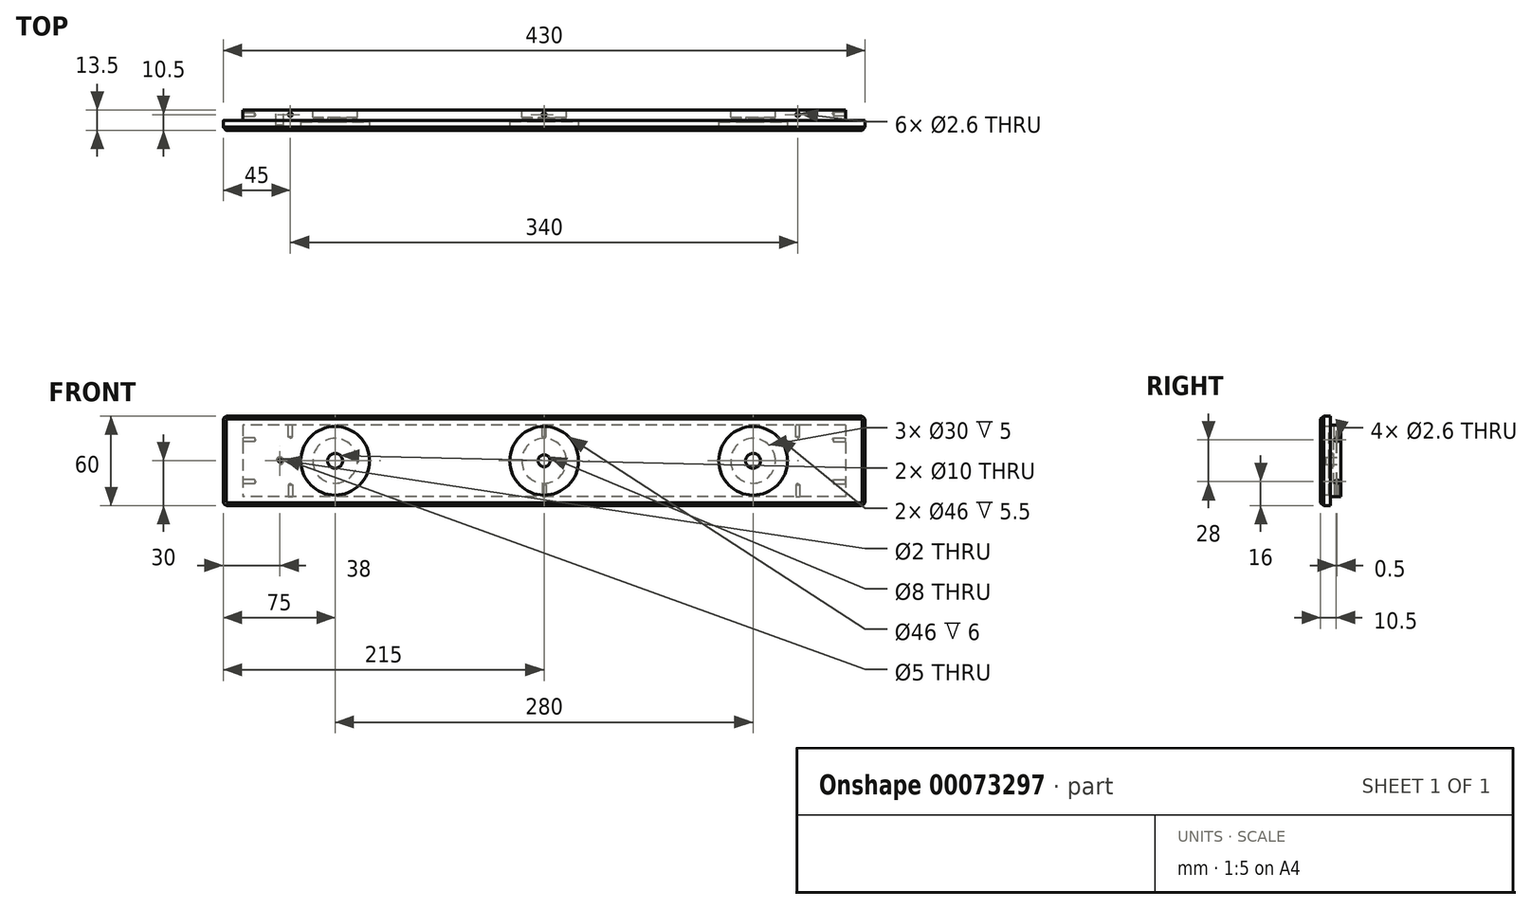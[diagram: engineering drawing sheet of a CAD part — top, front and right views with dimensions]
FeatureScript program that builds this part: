
annotation { "Feature Type Name" : "Feature", "Feature Type Description" : "" }
export const myFeature = defineFeature(function(context is Context, id is Id, definition is map)
    precondition{}
    {
        {
            var Q0;
            Q0=qCreatedBy(makeId("Right.planeOp"),FACE);
            var sketch = newSketch(context, id + "F0", { "sketchPlane" : qUnion([Q0])});
            skPoint(sketch, "E0.rect.middle", {"position": v(0, 0) * mm});
            skLineSegment(sketch, "E1.right", {"start": v(0, 30) * mm, "end": v(0, -30) * mm});
            skLineSegment(sketch, "E2", {"start": v(-6.5, 17.62) * mm, "end": v(-6.5, -17.62) * mm});
            skLineSegment(sketch, "E3", {"start": v(0, 30) * mm, "end": v(0, 24) * mm});
            skLineSegment(sketch, "E4", {"start": v(0, 24) * mm, "end": v(7, 24) * mm});
            skLineSegment(sketch, "E5.MirrorCS", {"start": v(0, -24) * mm, "end": v(7, -24) * mm});
            skLineSegment(sketch, "E6", {"start": v(7, -24) * mm, "end": v(7, 24) * mm});
            skLineSegment(sketch, "E7", {"start": v(0, -30) * mm, "end": v(-6.5, -30) * mm});
            skLineSegment(sketch, "E8", {"start": v(-6.5, -30) * mm, "end": v(-6.5, -16.02) * mm});
            skLineSegment(sketch, "E9", {"start": v(-6.5, 17.62) * mm, "end": v(-6.5, 30) * mm});
            skLineSegment(sketch, "E10", {"start": v(-6.5, 30) * mm, "end": v(0, 30) * mm});
            skSolve(sketch);
        }
        {
            var Q0;
            {var subQ2=sQuery(id+"F0.wireOp",EDGE,"E2");Q0=makeQuery(id+"F0.imprint","IMPRINT",FACE,{"disambiguationData":[TD([[makeQuery(id+"F0.imprint","IMPRINT",EDGE,{"derivedFrom":subQ2}),1.0]])]});}
            extrude(context, id + "F1", {"entities" : qUnion([Q0]), "endBound" : BoundingType.SYMMETRIC, "depth" : 430 * mm});
        }
        {
            var Q0;
            {var subQ2=sQuery(id+"F0.wireOp",EDGE,"E2");Q0=makeQuery(id+"F0.imprint","IMPRINT",FACE,{"disambiguationData":[TD([[makeQuery(id+"F0.imprint","IMPRINT",EDGE,{"derivedFrom":subQ2}),1.0]])]});}
            var Q1;
            {var subQ0=sQuery(id+"F0.wireOp",EDGE,"E4");Q1=makeQuery(id+"F0.imprint","IMPRINT",FACE,{"disambiguationData":[TD([[makeQuery(id+"F0.imprint","IMPRINT",EDGE,{"derivedFrom":subQ0}),-1.0]])]});}
            extrude(context, id + "F2", {"entities" : qUnion([Q0, Q1]), "operationType" : NewBodyOperationType.ADD, "endBound" : BoundingType.SYMMETRIC, "depth" : 404 * mm});
        }
        {
            var Q0;
            Q0=makeQuery(id+"F1.opExtrude","SWEPT_FACE",FACE,{"disambiguationData":[OSD([sQuery(id+"F0.wireOp",EDGE,"E2")])]});
            var sketch = newSketch(context, id + "F3", { "sketchPlane" : qUnion([Q0])});
            skPoint(sketch, "E11", {"position": v(0, 0) * mm});
            skPoint(sketch, "E12", {"position": v(140, 0) * mm});
            skPoint(sketch, "E13.MirrorP", {"position": v(-140, 0) * mm});
            skLineSegment(sketch, "E14", {"start": v(-140, 0) * mm, "end": v(-140, 63.96) * mm});
            skPoint(sketch, "E15", {"position": v(-140, 25) * mm});
            skLineSegment(sketch, "E16", {"start": v(-140, 0) * mm, "end": v(-215, 0) * mm});
            skPoint(sketch, "E17", {"position": v(-190, 0) * mm});
            skSolve(sketch);
        }
        {
            var Q0;
            Q0=sQuery(id+"F3.wireOp",VERTEX,"E11");
            var Q1;
            Q1=makeQuery(id+"F1.opExtrude","SWEPT_BODY",BODY,{"disambiguationData":[OSD([sQuery(id+"F0.wireOp",EDGE,"E1.right"),sQuery(id+"F0.wireOp",EDGE,"eec81103-8235-454d-a062-b2860544f3eb"),sQuery(id+"F0.wireOp",EDGE,"1854443f-789e-406a-befe-9d87532f86950.MirrorCS"),sQuery(id+"F0.wireOp",EDGE,"E2")])]});
            hole(context, id + "F4", {"style" : HoleStyle.C_BORE, "holeDiameter" : 8 * mm, "cBoreDiameter" : 46 * mm, "cBoreDepth" : 6 * mm, "endStyle" : HoleEndStyle.THROUGH, "locations" : qUnion([Q0]), "scope" : qUnion([Q1]), "tappedDepth" : 12 * mm, "tapClearance" : 3});
        }
        {
            var Q0;
            Q0=sQuery(id+"F3.wireOp",VERTEX,"E12");
            var Q1;
            Q1=sQuery(id+"F3.wireOp",VERTEX,"E13.MirrorP");
            var Q2;
            Q2=makeQuery(id+"F1.opExtrude","SWEPT_BODY",BODY,{"disambiguationData":[OSD([sQuery(id+"F0.wireOp",EDGE,"E1.right"),sQuery(id+"F0.wireOp",EDGE,"eec81103-8235-454d-a062-b2860544f3eb"),sQuery(id+"F0.wireOp",EDGE,"1854443f-789e-406a-befe-9d87532f86950.MirrorCS"),sQuery(id+"F0.wireOp",EDGE,"E2")])]});
            hole(context, id + "F5", {"style" : HoleStyle.C_BORE, "holeDiameter" : 10 * mm, "cBoreDiameter" : 46 * mm, "cBoreDepth" : 5.5 * mm, "endStyle" : HoleEndStyle.THROUGH, "locations" : qUnion([Q0, Q1]), "scope" : qUnion([Q2]), "tappedDepth" : 12 * mm, "tapClearance" : 3});
        }
        {
            var Q0;
            Q0=makeQuery(id+"F2.opExtrude","SWEPT_FACE",FACE,{"disambiguationData":[OSD([sQuery(id+"F0.wireOp",EDGE,"E5.MirrorCS")])]});
            var sketch = newSketch(context, id + "F6", { "sketchPlane" : qUnion([Q0])});
            skPoint(sketch, "E18", {"position": v(0, -4) * mm});
            skPoint(sketch, "E19", {"position": v(-170, -4) * mm});
            skPoint(sketch, "E20.MirrorP", {"position": v(170, -4) * mm});
            skSolve(sketch);
        }
        {
            var Q0;
            Q0=makeQuery(id+"F2.opExtrude","CAP_FACE",FACE,{"disambiguationData":[OSD([sQuery(id+"F0.wireOp",EDGE,"E1.right"),sQuery(id+"F0.wireOp",EDGE,"eec81103-8235-454d-a062-b2860544f3eb"),sQuery(id+"F0.wireOp",EDGE,"1854443f-789e-406a-befe-9d87532f86950.MirrorCS"),sQuery(id+"F0.wireOp",EDGE,"E2"),sQuery(id+"F0.wireOp",EDGE,"E3"),sQuery(id+"F0.wireOp",EDGE,"E4"),sQuery(id+"F0.wireOp",EDGE,"E5.MirrorCS"),sQuery(id+"F0.wireOp",EDGE,"E6")])],"isStart":false});
            var sketch = newSketch(context, id + "F7", { "sketchPlane" : qUnion([Q0])});
            skPoint(sketch, "E21", {"position": v(4.5, 14) * mm});
            skPoint(sketch, "E22.MirrorP", {"position": v(4.5, -14) * mm});
            skSolve(sketch);
        }
        {
            var Q0;
            Q0=makeQuery(id+"F2.opExtrude","CAP_FACE",FACE,{"disambiguationData":[OSD([sQuery(id+"F0.wireOp",EDGE,"E1.right"),sQuery(id+"F0.wireOp",EDGE,"eec81103-8235-454d-a062-b2860544f3eb"),sQuery(id+"F0.wireOp",EDGE,"1854443f-789e-406a-befe-9d87532f86950.MirrorCS"),sQuery(id+"F0.wireOp",EDGE,"E2"),sQuery(id+"F0.wireOp",EDGE,"E3"),sQuery(id+"F0.wireOp",EDGE,"E4"),sQuery(id+"F0.wireOp",EDGE,"E5.MirrorCS"),sQuery(id+"F0.wireOp",EDGE,"E6")])],"isStart":true});
            var sketch = newSketch(context, id + "F8", { "sketchPlane" : qUnion([Q0])});
            skPoint(sketch, "E23", {"position": v(-4, 14) * mm});
            skPoint(sketch, "E24.MirrorP", {"position": v(-4, -14) * mm});
            skSolve(sketch);
        }
        {
            var Q0;
            Q0=sQuery(id+"F8.wireOp",VERTEX,"E23");
            var Q1;
            Q1=sQuery(id+"F8.wireOp",VERTEX,"E24.MirrorP");
            var Q2;
            Q2=sQuery(id+"F6.wireOp",VERTEX,"E19");
            var Q3;
            Q3=sQuery(id+"F6.wireOp",VERTEX,"E18");
            var Q4;
            Q4=sQuery(id+"F6.wireOp",VERTEX,"E20.MirrorP");
            var Q5;
            Q5=sQuery(id+"F7.wireOp",VERTEX,"E22.MirrorP");
            var Q6;
            Q6=sQuery(id+"F7.wireOp",VERTEX,"E21");
            var Q7;
            Q7=makeQuery(id+"F1.opExtrude","SWEPT_BODY",BODY,{"disambiguationData":[OSD([sQuery(id+"F0.wireOp",EDGE,"E1.right"),sQuery(id+"F0.wireOp",EDGE,"eec81103-8235-454d-a062-b2860544f3eb"),sQuery(id+"F0.wireOp",EDGE,"1854443f-789e-406a-befe-9d87532f86950.MirrorCS"),sQuery(id+"F0.wireOp",EDGE,"E2"),sQuery(id+"F0.wireOp",EDGE,"E3")])]});
            hole(context, id + "F9", {"style" : HoleStyle.SIMPLE, "holeDiameter" : 2.6 * mm, "endStyle" : HoleEndStyle.BLIND, "holeDepth" : 8 * mm, "locations" : qUnion([Q0, Q1, Q2, Q3, Q4, Q5, Q6]), "scope" : qUnion([Q7]), "tappedDepth" : 12 * mm, "tapClearance" : 3});
        }
        {
            var Q0;
            Q0=makeQuery(id+"F1.opExtrude","CAP_EDGE",EDGE,{"disambiguationData":[OSD([sQuery(id+"F0.wireOp",EDGE,"jxey3gqm-EkgS-sKmh-oDEa-NIYkAWQqticZ")])],"isStart":true});
            var Q1;
            Q1=makeQuery(id+"F1.opExtrude","CAP_EDGE",EDGE,{"disambiguationData":[OSD([sQuery(id+"F0.wireOp",EDGE,"jxey3gqm-EkgS-sKmh-oDEa-NIYkAWQqticZ")])],"isStart":false});
            var Q2;
            Q2=makeQuery(id+"F1.opExtrude","CAP_EDGE",EDGE,{"disambiguationData":[OSD([sQuery(id+"F0.wireOp",EDGE,"E7")])],"isStart":false});
            var Q3;
            Q3=makeQuery(id+"F1.opExtrude","CAP_EDGE",EDGE,{"disambiguationData":[OSD([sQuery(id+"F0.wireOp",EDGE,"E7")])],"isStart":true});
            var Q4;
            Q4=makeQuery(id+"F1.opExtrude","CAP_EDGE",EDGE,{"disambiguationData":[OSD([sQuery(id+"F0.wireOp",EDGE,"E10")])],"isStart":false});
            var Q5;
            Q5=makeQuery(id+"F1.opExtrude","CAP_EDGE",EDGE,{"disambiguationData":[OSD([sQuery(id+"F0.wireOp",EDGE,"E10")])],"isStart":true});
            fillet(context, id + "F10", {"entities" : qUnion([Q0, Q1, Q2, Q3, Q4, Q5]), "radius" : 3 * mm, "tangentPropagation" : true, "allowEdgeOverflow" : false});
        }
        {
            var Q0;
            Q0=makeQuery(id+"F1.opExtrude","SWEPT_EDGE",EDGE,{"disambiguationData":[OSD([sQuery(id+"F0.wireOp",EDGE,"jxey3gqm-EkgS-sKmh-oDEa-NIYkAWQqticZ"),sQuery(id+"F0.wireOp",EDGE,"AvndLzNt-SVzn-5ECm-wgop-vTR7EgqtF20P")])]});
            var Q1;
            Q1=makeQuery(id+"F1.opExtrude","CAP_EDGE",EDGE,{"disambiguationData":[OSD([sQuery(id+"F0.wireOp",EDGE,"E2"),sQuery(id+"F0.wireOp",EDGE,"AvndLzNt-SVzn-5ECm-wgop-vTR7EgqtF20P"),sQuery(id+"F0.wireOp",EDGE,"E8")])],"isStart":true});
            var Q2;
            Q2=makeQuery(id+"F1.opExtrude","SWEPT_EDGE",EDGE,{"disambiguationData":[OSD([sQuery(id+"F0.wireOp",EDGE,"E7"),sQuery(id+"F0.wireOp",EDGE,"E8")])]});
            var Q3;
            Q3=makeQuery(id+"F1.opExtrude","CAP_EDGE",EDGE,{"disambiguationData":[OSD([sQuery(id+"F0.wireOp",EDGE,"E2"),sQuery(id+"F0.wireOp",EDGE,"AvndLzNt-SVzn-5ECm-wgop-vTR7EgqtF20P"),sQuery(id+"F0.wireOp",EDGE,"E8")])],"isStart":false});
            var Q4;
            Q4=makeQuery(id+"F1.opExtrude","SWEPT_EDGE",EDGE,{"disambiguationData":[OSD([sQuery(id+"F0.wireOp",EDGE,"E9"),sQuery(id+"F0.wireOp",EDGE,"E10")])]});
            chamfer(context, id + "F11", {"entities" : qUnion([Q0, Q1, Q2, Q3, Q4]), "width" : 2 * mm, "tangentPropagation" : true});
        }
        {
            var Q0;
            Q0=makeQuery(id+"F2.opExtrude","SWEPT_FACE",FACE,{"disambiguationData":[OSD([sQuery(id+"F0.wireOp",EDGE,"E4")])]});
            var sketch = newSketch(context, id + "F12", { "sketchPlane" : qUnion([Q0])});
            skPoint(sketch, "E25", {"position": v(0, 7) * mm});
            skPoint(sketch, "E26", {"position": v(0, 4) * mm});
            skPoint(sketch, "E26.positionSnap0", {"position": v(0, 0) * mm});
            skPoint(sketch, "E27.MirrorP", {"position": v(170, 4) * mm});
            skPoint(sketch, "E28", {"position": v(-170, 4) * mm});
            skSolve(sketch);
        }
        {
            var Q0;
            Q0=makeQuery(id+"F2.opExtrude","SWEPT_FACE",FACE,{"disambiguationData":[OSD([sQuery(id+"F0.wireOp",EDGE,"E6")])]});
            var sketch = newSketch(context, id + "F13", { "sketchPlane" : qUnion([Q0])});
            skPoint(sketch, "E29", {"position": v(-140, 0) * mm});
            skPoint(sketch, "E30", {"position": v(0, 0) * mm});
            skPoint(sketch, "E31", {"position": v(140, 0) * mm});
            skSolve(sketch);
        }
        {
            var Q0;
            Q0=sQuery(id+"F12.wireOp",VERTEX,"E26");
            var Q1;
            Q1=sQuery(id+"F12.wireOp",VERTEX,"E28");
            var Q2;
            Q2=sQuery(id+"F12.wireOp",VERTEX,"E27.MirrorP");
            var Q3;
            Q3=makeQuery(id+"F1.opExtrude","SWEPT_BODY",BODY,{"disambiguationData":[OSD([sQuery(id+"F0.wireOp",EDGE,"E1.right"),sQuery(id+"F0.wireOp",EDGE,"E2"),sQuery(id+"F0.wireOp",EDGE,"E3"),sQuery(id+"F0.wireOp",EDGE,"E7"),sQuery(id+"F0.wireOp",EDGE,"E8"),sQuery(id+"F0.wireOp",EDGE,"E9"),sQuery(id+"F0.wireOp",EDGE,"E10")])]});
            hole(context, id + "F14", {"style" : HoleStyle.SIMPLE, "endStyle" : HoleEndStyle.BLIND, "holeDiameter" : 2.6 * mm, "holeDepth" : 8 * mm, "tappedDepth" : 12 * mm, "tapClearance" : 3, "locations" : qUnion([Q0, Q1, Q2]), "scope" : qUnion([Q3])});
        }
        {
            var Q0;
            Q0=sQuery(id+"F13.wireOp",VERTEX,"E29");
            var Q1;
            Q1=sQuery(id+"F13.wireOp",VERTEX,"E30");
            var Q2;
            Q2=sQuery(id+"F13.wireOp",VERTEX,"E31");
            var Q3;
            Q3=makeQuery(id+"F1.opExtrude","SWEPT_BODY",BODY,{"disambiguationData":[OSD([sQuery(id+"F0.wireOp",EDGE,"E1.right"),sQuery(id+"F0.wireOp",EDGE,"E2"),sQuery(id+"F0.wireOp",EDGE,"E3"),sQuery(id+"F0.wireOp",EDGE,"E7"),sQuery(id+"F0.wireOp",EDGE,"E8"),sQuery(id+"F0.wireOp",EDGE,"E9"),sQuery(id+"F0.wireOp",EDGE,"E10")])]});
            hole(context, id + "F15", {"style" : HoleStyle.C_BORE, "endStyle" : HoleEndStyle.BLIND, "holeDiameter" : 8 * mm, "cBoreDiameter" : 30 * mm, "cBoreDepth" : 5 * mm, "holeDepth" : 14 * mm, "tappedDepth" : 12 * mm, "tapClearance" : 3, "locations" : qUnion([Q0, Q1, Q2]), "scope" : qUnion([Q3])});
        }
        {
            var Q0;
            Q0=makeQuery(id+"F2.opExtrude","SWEPT_FACE",FACE,{"disambiguationData":[OSD([sQuery(id+"F0.wireOp",EDGE,"E6")])]});
            var sketch = newSketch(context, id + "F16", { "sketchPlane" : qUnion([Q0])});
            skLineSegment(sketch, "E32", {"start": v(0, 0) * mm, "end": v(-202, 0) * mm});
            skLineSegment(sketch, "E33", {"start": v(-202, 0) * mm, "end": v(-176.22, 0) * mm});
            skLineSegment(sketch, "E34", {"start": v(0, 0) * mm, "end": v(202, 0) * mm});
            skPoint(sketch, "E35", {"position": v(177, 0) * mm});
            skSolve(sketch);
        }
        {
            var Q0;
            Q0=sQuery(id+"F16.wireOp",VERTEX,"E35");
            var Q1;
            Q1=makeQuery(id+"F1.opExtrude","SWEPT_BODY",BODY,{"disambiguationData":[OSD([sQuery(id+"F0.wireOp",EDGE,"E1.right"),sQuery(id+"F0.wireOp",EDGE,"E2"),sQuery(id+"F0.wireOp",EDGE,"E3"),sQuery(id+"F0.wireOp",EDGE,"E7"),sQuery(id+"F0.wireOp",EDGE,"E8"),sQuery(id+"F0.wireOp",EDGE,"E9"),sQuery(id+"F0.wireOp",EDGE,"E10")])]});
            hole(context, id + "F17", {"style" : HoleStyle.SIMPLE, "endStyle" : HoleEndStyle.THROUGH, "holeDiameter" : 2 * mm, "tappedDepth" : 12 * mm, "tapClearance" : 3, "locations" : qUnion([Q0]), "scope" : qUnion([Q1])});
        }
        {
            var Q0;
            Q0=makeQuery(id+"F2.opExtrude","SWEPT_FACE",FACE,{"disambiguationData":[OSD([sQuery(id+"F0.wireOp",EDGE,"E6")])]});
            var sketch = newSketch(context, id + "F18", { "sketchPlane" : qUnion([Q0])});
            skPoint(sketch, "E36", {"position": v(177, 0) * mm});
            skSolve(sketch);
        }
        {
            var Q0;
            Q0=sQuery(id+"F18.wireOp",VERTEX,"E36");
            var Q1;
            Q1=makeQuery(id+"F1.opExtrude","SWEPT_BODY",BODY,{"disambiguationData":[OSD([sQuery(id+"F0.wireOp",EDGE,"E1.right"),sQuery(id+"F0.wireOp",EDGE,"E2"),sQuery(id+"F0.wireOp",EDGE,"E3"),sQuery(id+"F0.wireOp",EDGE,"E7"),sQuery(id+"F0.wireOp",EDGE,"E8"),sQuery(id+"F0.wireOp",EDGE,"E9"),sQuery(id+"F0.wireOp",EDGE,"E10")])]});
            hole(context, id + "F19", {"style" : HoleStyle.SIMPLE, "endStyle" : HoleEndStyle.BLIND, "holeDiameter" : 5 * mm, "holeDepth" : 10 * mm, "tappedDepth" : 12 * mm, "tapClearance" : 3, "locations" : qUnion([Q0]), "scope" : qUnion([Q1])});
        }
    });
